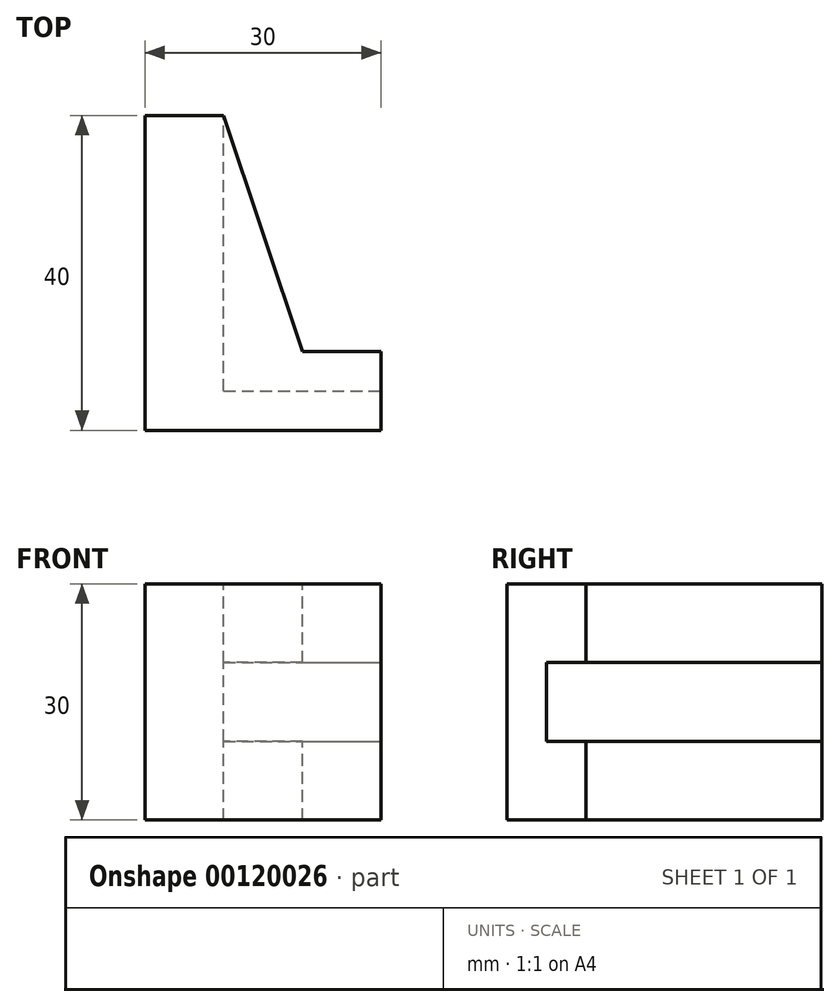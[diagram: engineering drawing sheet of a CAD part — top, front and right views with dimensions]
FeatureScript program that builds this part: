
annotation { "Feature Type Name" : "Feature", "Feature Type Description" : "" }
export const myFeature = defineFeature(function(context is Context, id is Id, definition is map)
    precondition{}
    {
        {
            var Q0;
            Q0=qCreatedBy(makeId("Top.planeOp"),FACE);
            var sketch = newSketch(context, id + "F0", { "sketchPlane" : qUnion([Q0])});
            skLineSegment(sketch, "E0", {"start": v(-40.79, -24.52) * mm, "end": v(-10.79, -24.52) * mm});
            skLineSegment(sketch, "E1", {"start": v(-10.79, -24.52) * mm, "end": v(-10.79, -14.52) * mm});
            skLineSegment(sketch, "E2", {"start": v(-10.79, -14.52) * mm, "end": v(-20.79, -14.52) * mm});
            skLineSegment(sketch, "E3", {"start": v(-30.79, 15.48) * mm, "end": v(-40.79, 15.48) * mm});
            skLineSegment(sketch, "E4", {"start": v(-40.79, 15.48) * mm, "end": v(-40.79, -24.52) * mm});
            skLineSegment(sketch, "E5", {"start": v(-30.79, 15.48) * mm, "end": v(-20.79, -14.52) * mm});
            skSolve(sketch);
        }
        {
            var Q0;
            Q0 = qSketchRegion(id + "F0", true);
            extrude(context, id + "F1", {"entities" : qUnion([Q0]), "oppositeDirection" : true, "depth" : 30 * mm});
        }
        {
            var Q0;
            Q0=makeQuery(id+"F1.opExtrude","SWEPT_FACE",FACE,{"disambiguationData":[OSD([sQuery(id+"F0.wireOp",EDGE,"E3")])]});
            var sketch = newSketch(context, id + "F2", { "sketchPlane" : qUnion([Q0])});
            skLineSegment(sketch, "E6.bottom", {"start": v(30.79, -10) * mm, "end": v(10.79, -10) * mm});
            skLineSegment(sketch, "E6.top", {"start": v(30.79, -20) * mm, "end": v(10.79, -20) * mm});
            skLineSegment(sketch, "E6.left", {"start": v(30.79, -10) * mm, "end": v(30.79, -20) * mm});
            skLineSegment(sketch, "E6.right", {"start": v(10.79, -10) * mm, "end": v(10.79, -20) * mm});
            skSolve(sketch);
        }
        {
            var Q0;
            Q0 = qSketchRegion(id + "F2", true);
            extrude(context, id + "F3", {"entities" : qUnion([Q0]), "operationType" : NewBodyOperationType.REMOVE, "oppositeDirection" : true, "depth" : 35 * mm});
        }
    });
